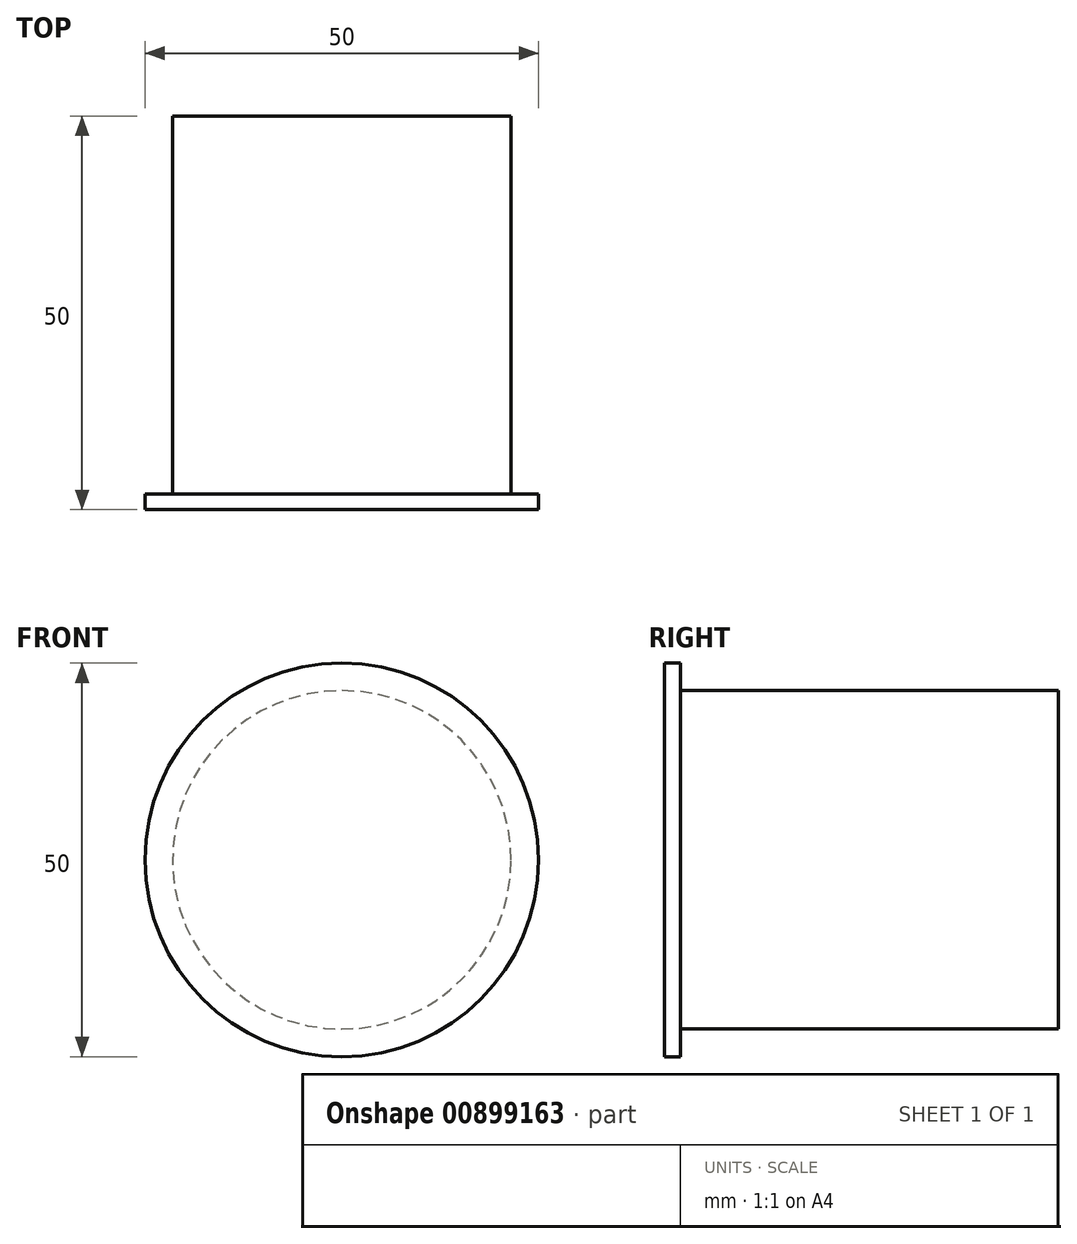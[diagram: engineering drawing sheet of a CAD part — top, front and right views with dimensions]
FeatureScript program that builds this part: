
annotation { "Feature Type Name" : "Feature", "Feature Type Description" : "" }
export const myFeature = defineFeature(function(context is Context, id is Id, definition is map)
    precondition{}
    {
        {
            var Q0;
            Q0=qCreatedBy(makeId("Top.planeOp"),FACE);
            var sketch = newSketch(context, id + "F0", { "sketchPlane" : qUnion([Q0])});
            skLineSegment(sketch, "E0", {"start": v(0, 0) * mm, "end": v(-25, 0) * mm});
            skLineSegment(sketch, "E1", {"start": v(-25, 0) * mm, "end": v(-25, 2) * mm});
            skLineSegment(sketch, "E2", {"start": v(-25, 2) * mm, "end": v(-21.5, 2) * mm});
            skLineSegment(sketch, "E3", {"start": v(-21.5, 2) * mm, "end": v(-21.5, 50) * mm});
            skLineSegment(sketch, "E4", {"start": v(-21.5, 50) * mm, "end": v(0, 50) * mm});
            skLineSegment(sketch, "E5", {"start": v(0, 50) * mm, "end": v(0, 0) * mm});
            skArc(sketch, "E6", {"start": v(0, -3.81) * mm, "mid": v(-6.6, -2.84) * mm, "end": v(-12.64, 0) * mm});
            skLineSegment(sketch, "E7", {"start": v(0, 0) * mm, "end": v(0, -3.81) * mm});
            skSolve(sketch);
        }
        {
            var Q0;
            {var subQ0=sQuery(id+"F0.wireOp",EDGE,"E1");Q0=makeQuery(id+"F0.imprint","IMPRINT",FACE,{"disambiguationData":[TD([[makeQuery(id+"F0.imprint","IMPRINT",EDGE,{"derivedFrom":subQ0}),-1.0]])]});}
            var Q1;
            {var subQ2=sQuery(id+"F0.wireOp",EDGE,"E6");Q1=makeQuery(id+"F0.imprint","IMPRINT",FACE,{"disambiguationData":[TD([[makeQuery(id+"F0.imprint","IMPRINT",EDGE,{"derivedFrom":subQ2}),-1.0]])]});}
            var Q2;
            Q2=sQuery(id+"F0.wireOp",EDGE,"E5");
            revolve(context, id + "F1", {"surfaceOperationType" : NewSurfaceOperationType.NEW, "entities" : qUnion([Q0, Q1]), "axis" : qUnion([Q2]), "revolveType" : RevolveType.FULL});
        }
    });
